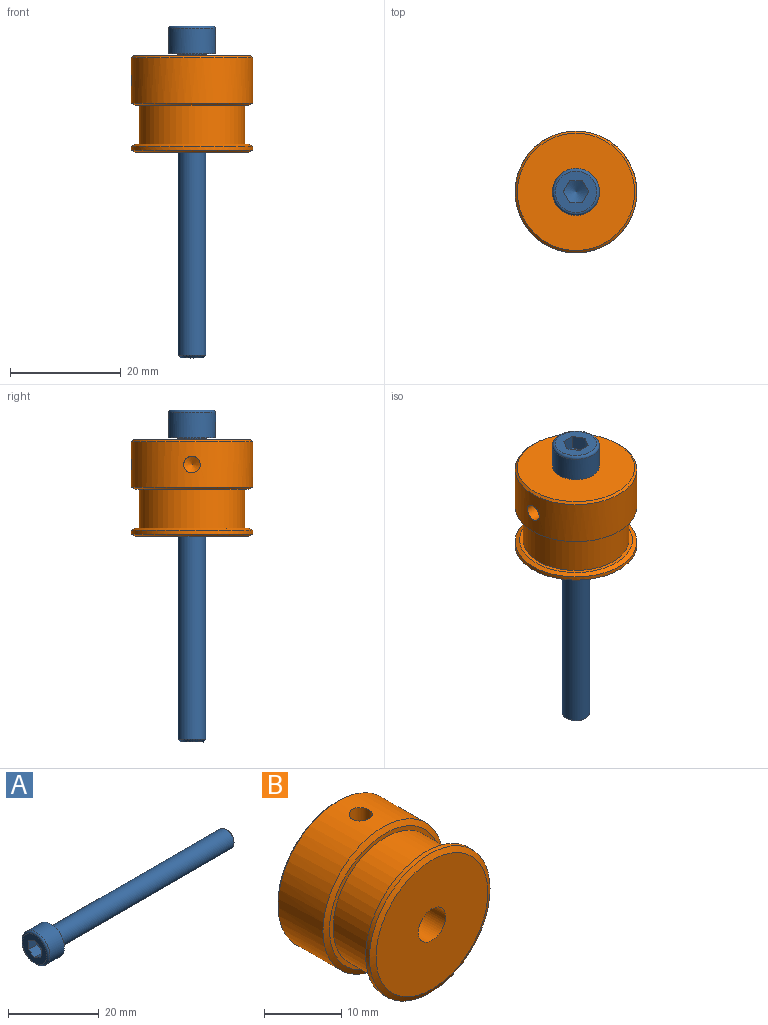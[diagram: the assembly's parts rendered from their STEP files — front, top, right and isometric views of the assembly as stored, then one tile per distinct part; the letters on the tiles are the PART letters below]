
ASSEMBLY  parts=2 mates=1
PART A: 15 faces, bbox 60x9.2x9.2 mm
  f0: torus R=2.7mm, axis (1,0,0), area 5.1mm2, adj f1,f2
  f1: cylinder r=2.5mm len=54.31mm, axis (1,0,0), area 853.1mm2, adj f0,f3
  f2: plane 8.5x8.5mm, normal (1,0,0), area 33.8mm2, adj f0,f7
  f3: cone r=2.25mm half-angle=45deg, axis (-1,0,0), area 9.8mm2, adj f1,f4
  f4: plane 4.02x4.02mm, normal (1,0,0), area 12.7mm2, adj f3
  f5: torus R=3.75mm, axis (1,0,0), area 20.1mm2, adj f6,f7
  f6: plane 7.5x7.5mm, normal (-1,0,0), area 30.3mm2, adj f5,f8,f9,f10,f11,f12,f13
  f7: cylinder r=4.25mm len=8.5mm, axis (1,0,0), area 120.2mm2, adj f2,f5
  f8: plane 2.76x2mm, normal (0,0.5,0.87), area 6mm2, adj f6,f9,f12,f14
  f9: plane 2.76x2mm, normal (0,-0.5,0.87), area 6mm2, adj f6,f8,f10,f14
  f10: plane 2.71x2.31mm, normal (0,-1,0), area 6mm2, adj f6,f9,f11,f14
  f11: plane 2.76x2mm, normal (0,-0.5,-0.87), area 6mm2, adj f6,f10,f13,f14
  f12: plane 2.76x2.31mm, normal (0,1,0), area 6mm2, adj f6,f8,f13,f14
  f13: plane 2.76x2mm, normal (0,0.5,-0.87), area 6mm2, adj f6,f11,f12,f14
  f14: cone r=1.15mm half-angle=60deg, axis (-1,0,0), area 16mm2, adj f8,f9,f10,f11,f12,f13
PART B: 16 faces, bbox 22x17.5x22 mm
  f0: cylinder r=11mm len=22mm, axis (0,1,0), area 552.6mm2, adj f8,f11,f12,f14
  f1: cylinder r=11mm len=22mm, axis (0,1,0), area 48.4mm2, adj f9,f10
  f2: plane 20.4x20.4mm, normal (0,-1,0), area 307.2mm2, adj f3,f10
  f3: cylinder r=2.5mm len=17.5mm, axis (0,1,0), area 274.9mm2, adj f2,f4
  f4: plane 21.2x21.2mm, normal (0,1,0), area 333.4mm2, adj f3,f11
  f5: plane 20.4x20.4mm, normal (0,-1,0), area 40.3mm2, adj f6,f8
  f6: cylinder r=9.55mm len=19.1mm, axis (0,1,0), area 420mm2, adj f5,f7
  f7: plane 20.4x20.4mm, normal (0,1,0), area 40.3mm2, adj f6,f9
  f8: cone r=11mm half-angle=63.4deg, axis (0,1,0), area 59.6mm2, adj f0,f5
  f9: cone r=10.2mm half-angle=63.4deg, axis (0,-1,0), area 59.6mm2, adj f1,f7
  f10: cone r=11mm half-angle=63.4deg, axis (0,1,0), area 59.6mm2, adj f1,f2
  f11: cone r=10.6mm half-angle=45deg, axis (0,-1,0), area 38.4mm2, adj f0,f4
  f12: cylinder r=1.5mm len=6.27mm, axis (0,0,1), area 58.6mm2, adj f0,f13
  f13: cone r=0mm half-angle=59deg, axis (0,0,1), area 8.2mm2, adj f12
  f14: cylinder r=1.5mm len=6.27mm, axis (1,0,0), area 58.6mm2, adj f0,f15
  f15: cone r=0mm half-angle=59deg, axis (1,0,0), area 8.2mm2, adj f14
PLACE A rot(axis=(0,1,0),90deg) t=(0,0,19.85)mm
PLACE B rot(axis=(0,-0.71,-0.71),180deg) t=(0,0,10.75)mm
MATE fastened A.f1 <-> B.f0  axis (0,0,-1) through (0,0,-7.5)mm
